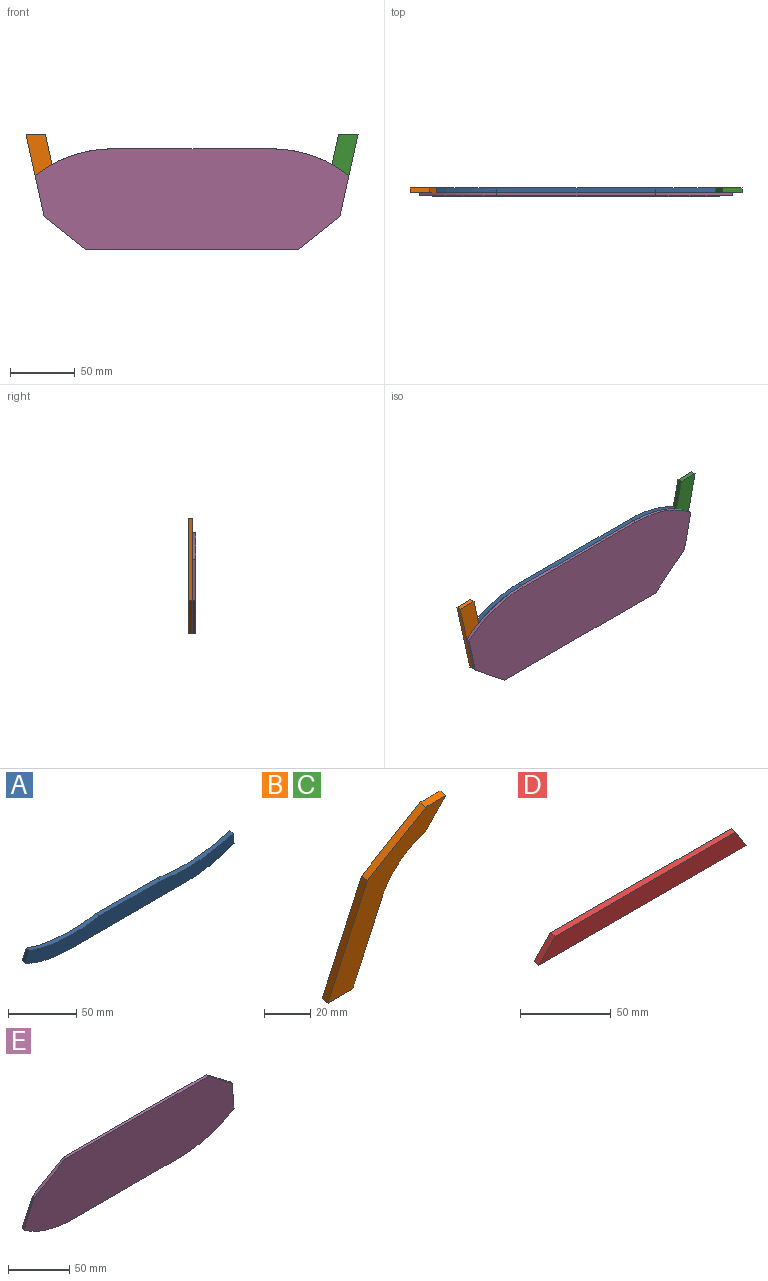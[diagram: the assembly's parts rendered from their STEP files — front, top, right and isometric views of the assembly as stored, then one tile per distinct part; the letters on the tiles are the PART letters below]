
ASSEMBLY  parts=5 mates=13
PART A: 10 faces, bbox 216.2x7.2x23.5 mm
  f0: plane 11.54x5.35mm, normal (0.98,-0.03,0.21), area 41.6mm2, adj f1,f7,f8,f9
  f1: cylinder r=97.5mm len=47.05mm, axis (0,-0.99,-0.16), area 179.9mm2, adj f0,f2,f8,f9
  f2: plane 122.12x3.62mm, normal (0,0.16,-0.99), area 447.4mm2, adj f1,f3,f8,f9
  f3: cylinder r=97.5mm len=47.05mm, axis (0,-0.99,-0.16), area 179.9mm2, adj f2,f4,f8,f9
  f4: plane 11.54x5.35mm, normal (-0.98,-0.03,0.21), area 41.6mm2, adj f3,f5,f8,f9
  f5: cylinder r=127mm len=73.9mm, axis (0,-0.99,-0.16), area 275.7mm2, adj f4,f6,f8,f9
  f6: plane 63.5x3.62mm, normal (0,-0.16,0.99), area 232.6mm2, adj f5,f7,f8,f9
  f7: cylinder r=127mm len=73.9mm, axis (0,-0.99,-0.16), area 275.7mm2, adj f0,f6,f8,f9
  f8: plane 216.21x22.92mm, normal (0,0.99,0.16), area 3231.2mm2, adj f0,f1,f2,f3,f4,f5,f6,f7
  f9: plane 216.21x22.92mm, normal (0,-0.99,-0.16), area 3231.2mm2, adj f0,f1,f2,f3,f4,f5,f6,f7
PART B: 9 faces, bbox 58x17.5x88.3 mm
  f0: plane 12.21x3.62mm, normal (0,-0.16,0.99), area 44.7mm2, adj f1,f6,f7,f8
  f1: plane 16.25x10.38mm, normal (0.84,0.09,-0.54), area 69.5mm2, adj f0,f2,f7,f8
  f2: cylinder r=34.19mm len=25.12mm, axis (0,-0.99,-0.16), area 126.9mm2, adj f1,f3,f7,f8
  f3: plane 48.1x11.15mm, normal (0.98,0.03,-0.21), area 180.5mm2, adj f2,f4,f7,f8
  f4: plane 15.01x3.62mm, normal (0,0.16,-0.99), area 55mm2, adj f3,f5,f7,f8
  f5: plane 63.29x14.04mm, normal (-0.98,-0.03,0.21), area 238.3mm2, adj f4,f6,f7,f8
  f6: plane 31.75x25.6mm, normal (-0.62,-0.12,0.77), area 148.8mm2, adj f0,f5,f7,f8
  f7: plane 87.75x58.01mm, normal (0,0.99,0.16), area 1426.8mm2, adj f0,f1,f2,f3,f4,f5,f6
  f8: plane 87.75x58.01mm, normal (0,-0.99,-0.16), area 1426.8mm2, adj f0,f1,f2,f3,f4,f5,f6
PART C: same geometry as B
PART D: 6 faces, bbox 161.2x6.1x16.3 mm
  f0: plane 161.19x3.62mm, normal (0,0.16,-0.99), area 590.5mm2, adj f1,f3,f4,f5
  f1: plane 16.25x10.38mm, normal (-0.84,-0.09,0.54), area 69.5mm2, adj f0,f2,f4,f5
  f2: plane 140.43x3.62mm, normal (0,-0.16,0.99), area 514.5mm2, adj f1,f3,f4,f5
  f3: plane 16.25x10.38mm, normal (0.84,-0.09,0.54), area 69.5mm2, adj f0,f2,f4,f5
  f4: plane 161.19x15.68mm, normal (0,0.99,0.16), area 2394.1mm2, adj f0,f1,f2,f3
  f5: plane 161.19x15.68mm, normal (0,-0.99,-0.16), area 2394.1mm2, adj f0,f1,f2,f3
PART E: 10 faces, bbox 242.4x14.6x77.3 mm
  f0: plane 164.86x2.41mm, normal (0,-0.16,0.99), area 402.6mm2, adj f1,f7,f8,f9
  f1: plane 31.75x25.41mm, normal (0.62,-0.12,0.77), area 99.2mm2, adj f0,f2,f8,f9
  f2: plane 31.74x7.38mm, normal (0.98,-0.03,0.21), area 79.4mm2, adj f1,f3,f8,f9
  f3: cylinder r=97.5mm len=60.14mm, axis (0,-0.99,-0.16), area 158.3mm2, adj f2,f4,f8,f9
  f4: plane 122.12x2.41mm, normal (0,0.16,-0.99), area 298.2mm2, adj f3,f5,f8,f9
  f5: cylinder r=97.5mm len=60.14mm, axis (0,-0.99,-0.16), area 158.3mm2, adj f4,f6,f8,f9
  f6: plane 31.74x7.38mm, normal (-0.98,-0.03,0.21), area 79.4mm2, adj f5,f7,f8,f9
  f7: plane 31.75x25.41mm, normal (-0.62,-0.12,0.77), area 99.2mm2, adj f0,f6,f8,f9
  f8: plane 242.4x76.89mm, normal (0,0.99,0.16), area 16693.8mm2, adj f0,f1,f2,f3,f4,f5,f6,f7
  f9: plane 242.4x76.89mm, normal (0,-0.99,-0.16), area 16693.8mm2, adj f0,f1,f2,f3,f4,f5,f6,f7
PLACE A rot(axis=(1,0,0),171deg) t=(0,1.83,88.84)mm
PLACE B rot(axis=(1,0,0),171deg) t=(0,1.83,88.84)mm
PLACE C rot(axis=(0,1,0.08),180deg) t=(0,-1.83,88.84)mm
PLACE D rot(axis=(1,0,0),171deg) t=(0,1.83,88.84)mm
PLACE E rot(axis=(1,0,0),171deg) t=(0,-1.83,88.84)mm
MATE planar D.f2 <-> E.f0  axis (0,0,-1) through (0,0,0)mm
MATE planar A.f4 <-> B.f3  axis (-0.98,0,-0.22) through (-106.88,0,60.2)mm
MATE planar A.f0 <-> C.f3  axis (0.98,0,-0.22) through (106.88,0,60.2)mm
MATE planar E.f9 <-> B.f7  axis (0,1,0) through (0,-1.83,39.43)mm
MATE planar E.f9 <-> D.f4  axis (0,1,0) through (0,-1.83,39.43)mm
MATE planar B.f0 <-> D.f2  axis (0,0,-1) through (-76.32,0,0)mm
MATE planar A.f8 <-> E.f9  axis (0,-1,0) through (-31.75,-1.83,60.75)mm
MATE planar E.f6 <-> B.f5  axis (-0.98,0,-0.22) through (-117.69,-3.05,41.21)mm
MATE planar C.f0 <-> D.f2  axis (0,0,-1) through (76.32,0,0)mm
MATE planar E.f9 <-> C.f8  axis (0,1,0) through (0,-1.83,39.43)mm
MATE planar B.f1 <-> D.f1  axis (0.84,0,0.55) through (-75.41,0,7.94)mm
MATE planar C.f1 <-> D.f3  axis (-0.84,0,0.55) through (75.41,0,7.94)mm
MATE planar E.f0 <-> D.f2  axis (0,0,-1) through (0,-3.05,0)mm
